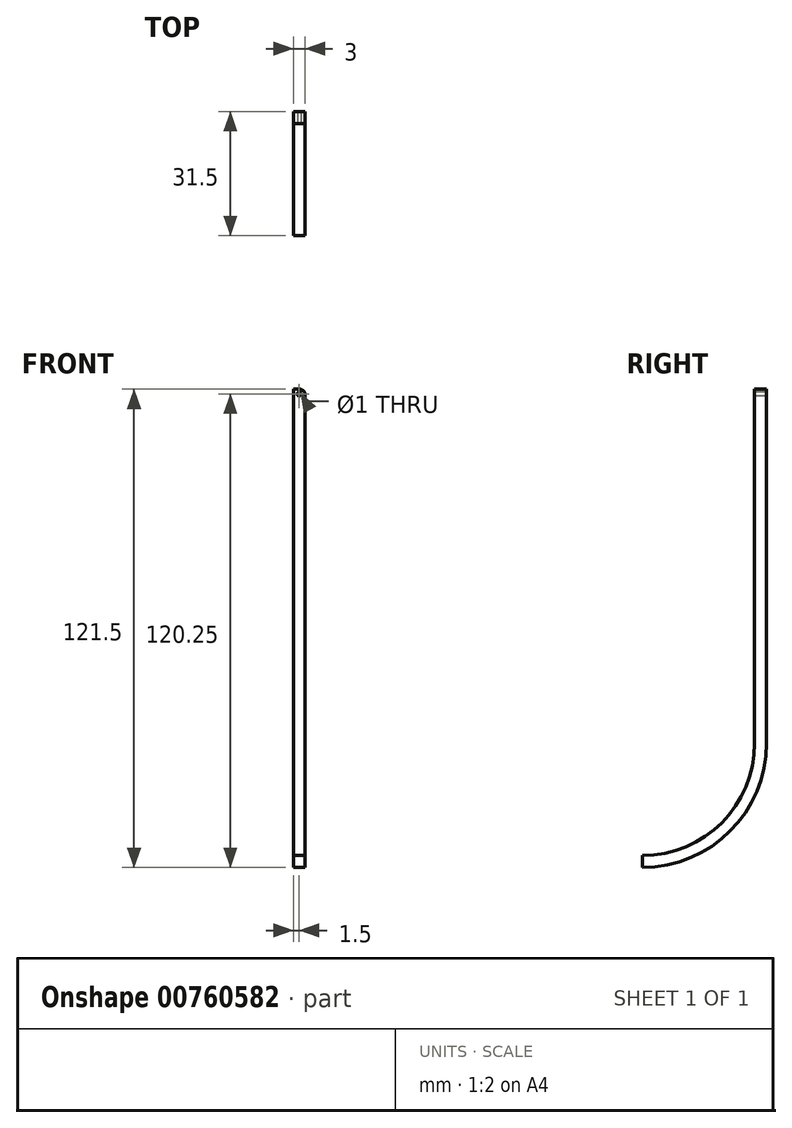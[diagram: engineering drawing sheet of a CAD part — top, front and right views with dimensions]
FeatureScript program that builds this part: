
annotation { "Feature Type Name" : "Feature", "Feature Type Description" : "" }
export const myFeature = defineFeature(function(context is Context, id is Id, definition is map)
    precondition{}
    {
        {
            var Q0;
            Q0=qCreatedBy(makeId("Right.planeOp"),FACE);
            var sketch = newSketch(context, id + "F0", { "sketchPlane" : qUnion([Q0])});
            skLineSegment(sketch, "E0", {"start": v(-1.5, 0) * mm, "end": v(1.5, 0) * mm});
            skLineSegment(sketch, "E1", {"start": v(1.5, 0) * mm, "end": v(1.5, -90) * mm});
            skLineSegment(sketch, "E2", {"start": v(-1.5, -90) * mm, "end": v(-1.5, 0) * mm});
            skLineSegment(sketch, "E3", {"start": v(-30, -118.5) * mm, "end": v(-30, -121.5) * mm});
            skArc(sketch, "E4", {"start": v(-1.5, -90) * mm, "mid": v(-9.85, -110.15) * mm, "end": v(-30, -118.5) * mm});
            skArc(sketch, "E5", {"start": v(1.5, -90) * mm, "mid": v(-7.73, -112.27) * mm, "end": v(-30, -121.5) * mm});
            skPoint(sketch, "E6.end.orphan", {"position": v(-1.5, -120) * mm});
            skSolve(sketch);
        }
        {
            var Q0;
            Q0=qCreatedBy(makeId("Front.planeOp"),FACE);
            var sketch = newSketch(context, id + "F1", { "sketchPlane" : qUnion([Q0])});
            skCircle(sketch, "E7", {"center": v(1.5, -1.25) * mm, "radius": 0.5 * mm});
            skSolve(sketch);
        }
        {
            var Q0;
            Q0 = qSketchRegion(id + "F0", true);
            extrude(context, id + "F2", {"entities" : qUnion([Q0]), "depth" : 3 * mm, "offsetDistance" : 25 * mm});
        }
        {
            var Q0;
            Q0 = qSketchRegion(id + "F1", true);
            extrude(context, id + "F3", {"entities" : qUnion([Q0]), "operationType" : NewBodyOperationType.REMOVE, "oppositeDirection" : true, "depth" : 1.5 * mm, "offsetDistance" : 25 * mm});
        }
        {
            var Q0;
            Q0 = qSketchRegion(id + "F1", true);
            extrude(context, id + "F4", {"entities" : qUnion([Q0]), "operationType" : NewBodyOperationType.REMOVE, "depth" : 1.5 * mm, "offsetDistance" : 25 * mm});
        }
        {
            var Q0;
            Q0=makeQuery(id+"F2.opExtrude","CAP_EDGE",EDGE,{"disambiguationData":[OSD([sQuery(id+"F0.wireOp",EDGE,"E0")])],"isStart":false});
            fillet(context, id + "F5", {"entities" : qUnion([Q0]), "radius" : 1.5 * mm, "tangentPropagation" : true, "allowEdgeOverflow" : false});
        }
    });
